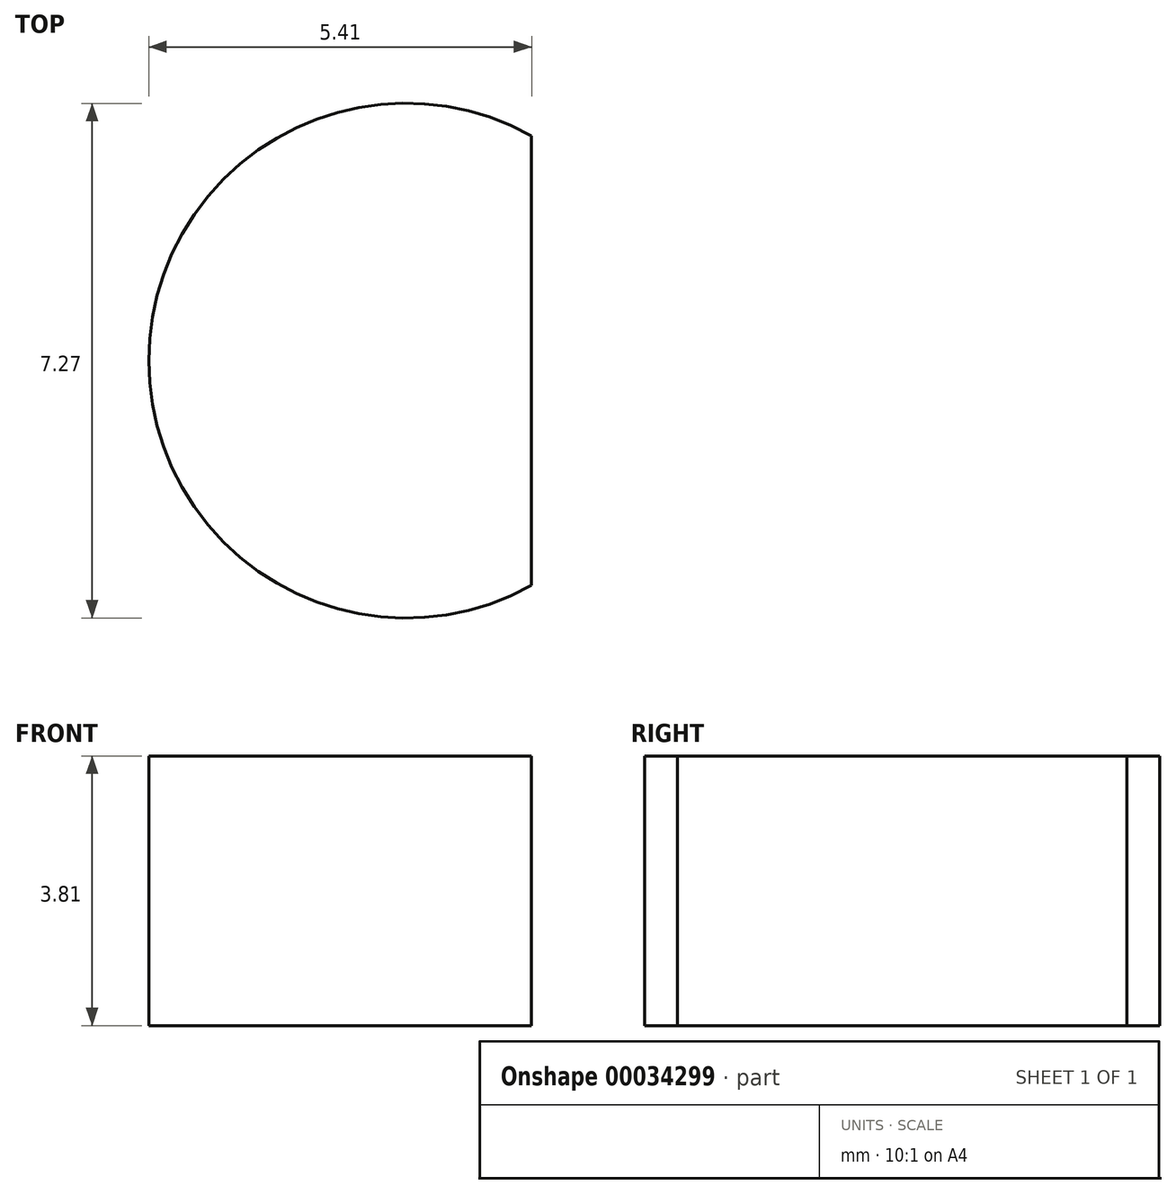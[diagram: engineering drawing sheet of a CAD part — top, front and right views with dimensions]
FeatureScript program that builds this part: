
annotation { "Feature Type Name" : "Feature", "Feature Type Description" : "" }
export const myFeature = defineFeature(function(context is Context, id is Id, definition is map)
    precondition{}
    {
        {
            var Q0;
            Q0=qCreatedBy(makeId("Top.planeOp"),FACE);
            var sketch = newSketch(context, id + "F0", { "sketchPlane" : qUnion([Q0])});
            skLineSegment(sketch, "E0", {"start": v(-32.88, 5.21) * mm, "end": v(-32.88, -1.14) * mm});
            skArc(sketch, "E1", {"start": v(-32.88, 5.21) * mm, "mid": v(-38.3, 2.04) * mm, "end": v(-32.88, -1.14) * mm});
            skSolve(sketch);
        }
        {
            var Q0;
            Q0=makeQuery(id+"F0.imprint","IMPRINT",FACE,{"disambiguationData":[TD([[makeQuery(id+"F0.imprint","IMPRINT",EDGE,{"derivedFrom":sQuery(id+"F0.wireOp",EDGE,"E0")}),-1.0]])]});
            extrude(context, id + "F1", {"entities" : qUnion([Q0]), "depth" : 3.8 * mm});
        }
    });
